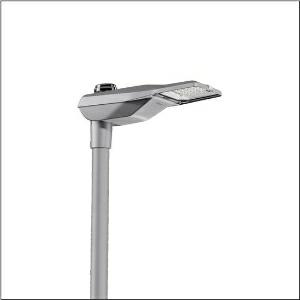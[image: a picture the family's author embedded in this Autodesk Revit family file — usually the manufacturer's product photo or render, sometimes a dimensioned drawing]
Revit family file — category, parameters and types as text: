
# Revit family: streetlight_sl_21_micro___p0_8a_5xe5u67n08db_bec5
name_source: partatom
category: Lighting Fixtures
units: mm (PartAtom-declared; Revit-internal decimal feet)

## family parameters
Cut with Voids When Loaded = No
Host = Face
Light Source = No
Part Type = Normal
Room Calculation Point = No
Round Connector Dimension = Use Diameter
Shared = No

## types (1)
- --- (1 x LED, 4520 lm, 39.1 W, 2700K)
    Apparent Load = 39 VA
    CIE Flux Codes = 33 69 96 100 100
    Color Rendering = 70
    Color Temperature = 2700K
    Default Elevation = 1800 mm
    Description = Streetlight SL 21 micro, mast luminaire, primary light control with lens, of PMMA, primary optical cover: cover, of toughened safety glass, transparent, light distribution: P0.8a, light emission: direct distribution, primary light characteristic: asymmetric, installation type: post-top, LED, 3G 1.5mm², High Power LED, rated luminous flux: 4.520lm, luminous efficacy: 116lm/W, light colour: 727, colour temperature: 2700K, control gear: NEMA (7pin), control: flexible luminous flux parameterisation, time-dependent luminous flux control, constant luminous flux control, pre-setting: linear dimming characteristic, overheat protection, mains connection: 230..240V, AC, 50/60Hz, connection cable pre-assembled, cable length: 6,5m, wiring characteristics: H07RN-F, start of lifetime: 39W, end of service life: 41W, reduction: 18W, luminaire housing, of diecast aluminium (EN AC-44300), powder-coated, Siteco® metallic grey (DB 702S), corrosivity category C5 mid according to DIN EN ISO 12944, multi-level sealing system, sealing non-destructively replaceable, inclination adjustable: 0°, 5°, 10°, 15°, length: 528mm, width: 235mm, height: 110mm, spigot size: 76/60mm (post-top), mounting height: 4..8m, protection rating (complete): IP66, insulation class (complete): insulation class I (protective earthing), certification: CE, ENEC, ENEC+, VDE, impact resistance: IK10, permissible operating ambient temperature for outdoor applications: -40..+50°C, standard-compliant lighting for roads and squares, packaging unit: 1 piece

Light Distribution: P0.8a
    Height = 110 mm
    Lamp = 1 x LED
    Lamp Light Flux = 4520 lm
    Lamp Power = 39.1 W
    Lamp count = 1
    Length = 528 mm
    Luminous efficacy = 116 lm/W
    Manufacturer = Siteco
    ModVariant = No
    Model = 5XE5U67N08DB
    Number of Poles = 1
    OnlyDefault = Yes
    Power Factor = 1
    Product Name = Streetlight SL 21 micro | P0.8a
    Product group = mast luminaire | pylon top
    ProductGroupID = 6100
    Protection Class = Protection class I
    Protection Degree = IP 66
    RLX_Detail_Level = 1
    RLX_Emergency_Light_Flux = 0 lm
    RLX_Emergency_Type = 0
    RLX_Emergency_Type_DB = No
    RlxData = <blob elided: 99281 chars, md5=f97cbd53>
    Socket = socket
    Standby Power = 0 W
    System Light Flux = 4520 lm
    System Power = 39 W
    Type Comments = factory setting: luminous flux: 100 % | dim-lin: 254 | 765 mA
    Type Image = l_1294375.jpg
    URL = http://relux.com
    VarID = @adj_073660
    Voltage = 0 V
    Weight = 0.00 kg
    Width = 235 mm

## geometry (parser evidence)
native form markers: Blend x4, Sweep x9
no freeform markers — native parametric forms only
